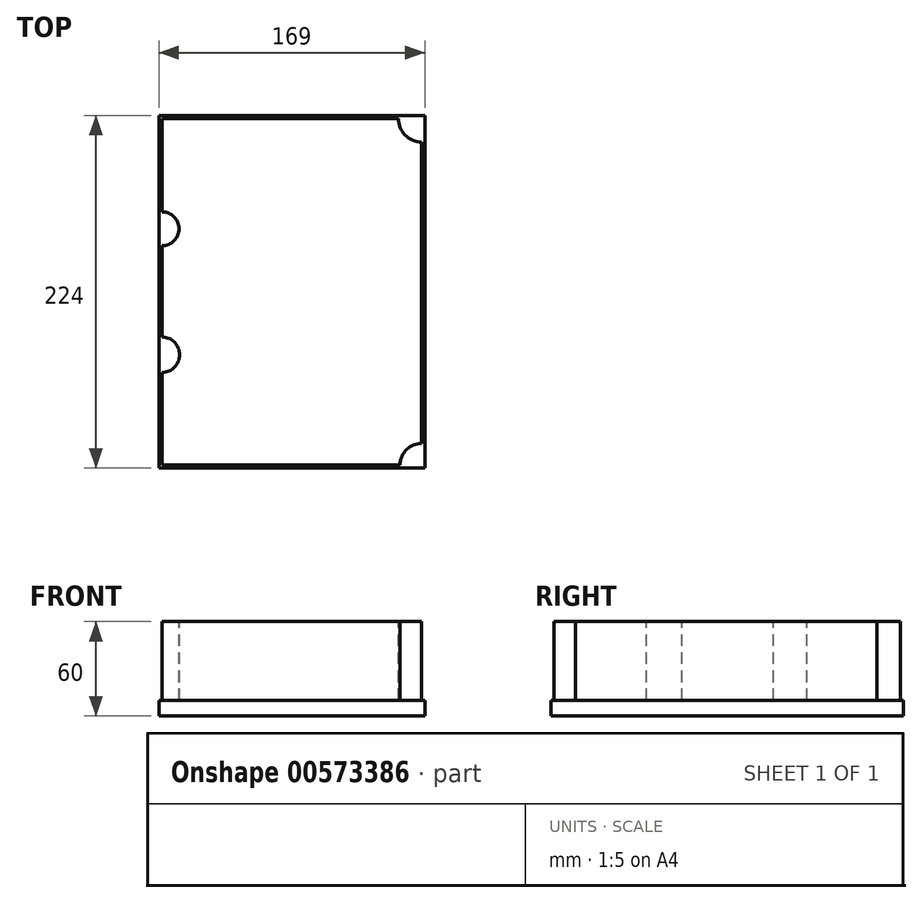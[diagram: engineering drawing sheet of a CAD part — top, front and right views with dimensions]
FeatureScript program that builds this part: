
annotation { "Feature Type Name" : "Feature", "Feature Type Description" : "" }
export const myFeature = defineFeature(function(context is Context, id is Id, definition is map)
    precondition{}
    {
        {
            var Q0;
            Q0=qCreatedBy(makeId("Top.planeOp"),FACE);
            var sketch = newSketch(context, id + "F0", { "sketchPlane" : qUnion([Q0])});
            skLineSegment(sketch, "E0.bottom", {"start": v(-181.19, 94.47) * mm, "end": v(-16.19, 94.47) * mm});
            skLineSegment(sketch, "E0.top", {"start": v(-181.19, -125.53) * mm, "end": v(-16.19, -125.53) * mm});
            skLineSegment(sketch, "E0.left", {"start": v(-181.19, 94.47) * mm, "end": v(-181.19, -125.53) * mm});
            skLineSegment(sketch, "E0.right", {"start": v(-16.19, 94.47) * mm, "end": v(-16.19, -125.53) * mm});
            skSolve(sketch);
        }
        {
            var Q0;
            Q0 = qSketchRegion(id + "F0", true);
            extrude(context, id + "F1", {"entities" : qUnion([Q0]), "depth" : 50 * mm, "offsetDistance" : 25 * mm});
        }
        {
            var Q0;
            Q0=makeQuery(id+"F1.opExtrude","CAP_FACE",FACE,{"disambiguationData":[OSD([sQuery(id+"F0.wireOp",EDGE,"E0.bottom"),sQuery(id+"F0.wireOp",EDGE,"E0.top"),sQuery(id+"F0.wireOp",EDGE,"E0.left"),sQuery(id+"F0.wireOp",EDGE,"E0.right")])],"isStart":false});
            var sketch = newSketch(context, id + "F2", { "sketchPlane" : qUnion([Q0])});
            skCircle(sketch, "E1", {"center": v(-16.19, 94.47) * mm, "radius": 14.84 * mm});
            skCircle(sketch, "E2", {"center": v(-16.19, -125.53) * mm, "radius": 13.74 * mm});
            skPoint(sketch, "E3.end.orphan", {"position": v(-278.26, 94.47) * mm});
            skCircle(sketch, "E4", {"center": v(-181.19, 24.47) * mm, "radius": 11.75 * mm});
            skPoint(sketch, "E5.start.orphan", {"position": v(-278.26, 24.47) * mm});
            skSolve(sketch);
        }
        {
            var Q0;
            {var subQ0=sQuery(id+"F2.wireOp",EDGE,"E2");var subQ1=makeQuery(id+"F1.opExtrude","CAP_EDGE",EDGE,{"disambiguationData":[OSD([sQuery(id+"F0.wireOp",EDGE,"E0.top")])],"isStart":false});var subQ2=makeQuery(id+"F2.imprint","INTERSECT",VERTEX,{"derivedFrom":[subQ1,subQ0]});Q0=makeQuery(id+"F2.imprint","IMPRINT",FACE,{"disambiguationData":[TD([[makeQuery(id+"F2.imprint","IMPRINT",EDGE,{"disambiguationData":[TD([[subQ2,-1.0]])],"derivedFrom":subQ0}),1.0]])]});}
            var Q1;
            {var subQ0=sQuery(id+"F2.wireOp",EDGE,"E1");var subQ1=makeQuery(id+"F1.opExtrude","CAP_EDGE",EDGE,{"disambiguationData":[OSD([sQuery(id+"F0.wireOp",EDGE,"E0.bottom")])],"isStart":false});var subQ2=makeQuery(id+"F2.imprint","INTERSECT",VERTEX,{"derivedFrom":[subQ1,subQ0]});Q1=makeQuery(id+"F2.imprint","IMPRINT",FACE,{"disambiguationData":[TD([[makeQuery(id+"F2.imprint","IMPRINT",EDGE,{"disambiguationData":[TD([[subQ2,1.0]])],"derivedFrom":subQ0}),1.0]])]});}
            var Q2;
            {var subQ0=sQuery(id+"F2.wireOp",EDGE,"E2");var subQ1=makeQuery(id+"F1.opExtrude","CAP_EDGE",EDGE,{"disambiguationData":[OSD([sQuery(id+"F0.wireOp",EDGE,"E0.top")])],"isStart":false});var subQ2=makeQuery(id+"F2.imprint","INTERSECT",VERTEX,{"derivedFrom":[subQ1,subQ0]});Q2=makeQuery(id+"F2.imprint","IMPRINT",FACE,{"disambiguationData":[TD([[makeQuery(id+"F2.imprint","IMPRINT",EDGE,{"disambiguationData":[TD([[subQ2,1.0]])],"derivedFrom":subQ0}),1.0]])]});}
            var Q3;
            {var subQ0=sQuery(id+"F2.wireOp",EDGE,"E1");var subQ1=makeQuery(id+"F1.opExtrude","CAP_EDGE",EDGE,{"disambiguationData":[OSD([sQuery(id+"F0.wireOp",EDGE,"E0.bottom")])],"isStart":false});var subQ2=makeQuery(id+"F2.imprint","INTERSECT",VERTEX,{"derivedFrom":[subQ1,subQ0]});Q3=makeQuery(id+"F2.imprint","IMPRINT",FACE,{"disambiguationData":[TD([[makeQuery(id+"F2.imprint","IMPRINT",EDGE,{"disambiguationData":[TD([[subQ2,-1.0]])],"derivedFrom":subQ0}),1.0]])]});}
            extrude(context, id + "F3", {"entities" : qUnion([Q0, Q1, Q2, Q3]), "operationType" : NewBodyOperationType.REMOVE, "oppositeDirection" : true, "depth" : 50 * mm, "offsetDistance" : 25 * mm});
        }
        {
            var Q0;
            Q0=makeQuery(id+"F1.opExtrude","CAP_FACE",FACE,{"disambiguationData":[OSD([sQuery(id+"F0.wireOp",EDGE,"E0.bottom"),sQuery(id+"F0.wireOp",EDGE,"E0.top"),sQuery(id+"F0.wireOp",EDGE,"E0.left"),sQuery(id+"F0.wireOp",EDGE,"E0.right")])],"isStart":false});
            var sketch = newSketch(context, id + "F4", { "sketchPlane" : qUnion([Q0])});
            skCircle(sketch, "E6", {"center": v(-181.19, 24.47) * mm, "radius": 10.78 * mm});
            skCircle(sketch, "E7", {"center": v(-181.19, -55.53) * mm, "radius": 11.2 * mm});
            skSolve(sketch);
        }
        {
            var Q0;
            Q0 = qSketchRegion(id + "F4", true);
            extrude(context, id + "F5", {"entities" : qUnion([Q0]), "operationType" : NewBodyOperationType.REMOVE, "oppositeDirection" : true, "depth" : 50 * mm, "offsetDistance" : 25 * mm});
        }
        {
            var Q0;
            Q0=makeQuery(id+"F1.opExtrude","CAP_FACE",FACE,{"disambiguationData":[OSD([sQuery(id+"F0.wireOp",EDGE,"E0.bottom"),sQuery(id+"F0.wireOp",EDGE,"E0.top"),sQuery(id+"F0.wireOp",EDGE,"E0.left"),sQuery(id+"F0.wireOp",EDGE,"E0.right")])],"isStart":true});
            var sketch = newSketch(context, id + "F6", { "sketchPlane" : qUnion([Q0])});
            skLineSegment(sketch, "E8", {"start": v(-181.19, 127.53) * mm, "end": v(-14.19, 127.53) * mm});
            skLineSegment(sketch, "E9", {"start": v(-181.19, 127.53) * mm, "end": v(-183.19, 127.53) * mm});
            skLineSegment(sketch, "E10", {"start": v(-183.19, 125.53) * mm, "end": v(-183.19, 127.53) * mm});
            skLineSegment(sketch, "E11", {"start": v(-183.19, 125.53) * mm, "end": v(-183.19, -96.47) * mm});
            skLineSegment(sketch, "E12", {"start": v(-159.2, -96.47) * mm, "end": v(-183.19, -96.47) * mm});
            skLineSegment(sketch, "E13", {"start": v(-159.2, -96.47) * mm, "end": v(-14.19, -96.47) * mm});
            skLineSegment(sketch, "E14", {"start": v(-14.19, -65.4) * mm, "end": v(-14.19, -96.47) * mm});
            skLineSegment(sketch, "E15", {"start": v(-14.19, -65.4) * mm, "end": v(-14.19, 127.53) * mm});
            skPoint(sketch, "E16.orphan", {"position": v(0, 127.53) * mm});
            skSolve(sketch);
        }
        {
            var Q0;
            Q0 = qSketchRegion(id + "F6", true);
            extrude(context, id + "F7", {"entities" : qUnion([Q0]), "operationType" : NewBodyOperationType.ADD, "depth" : 10 * mm, "offsetDistance" : 25 * mm});
        }
    });
